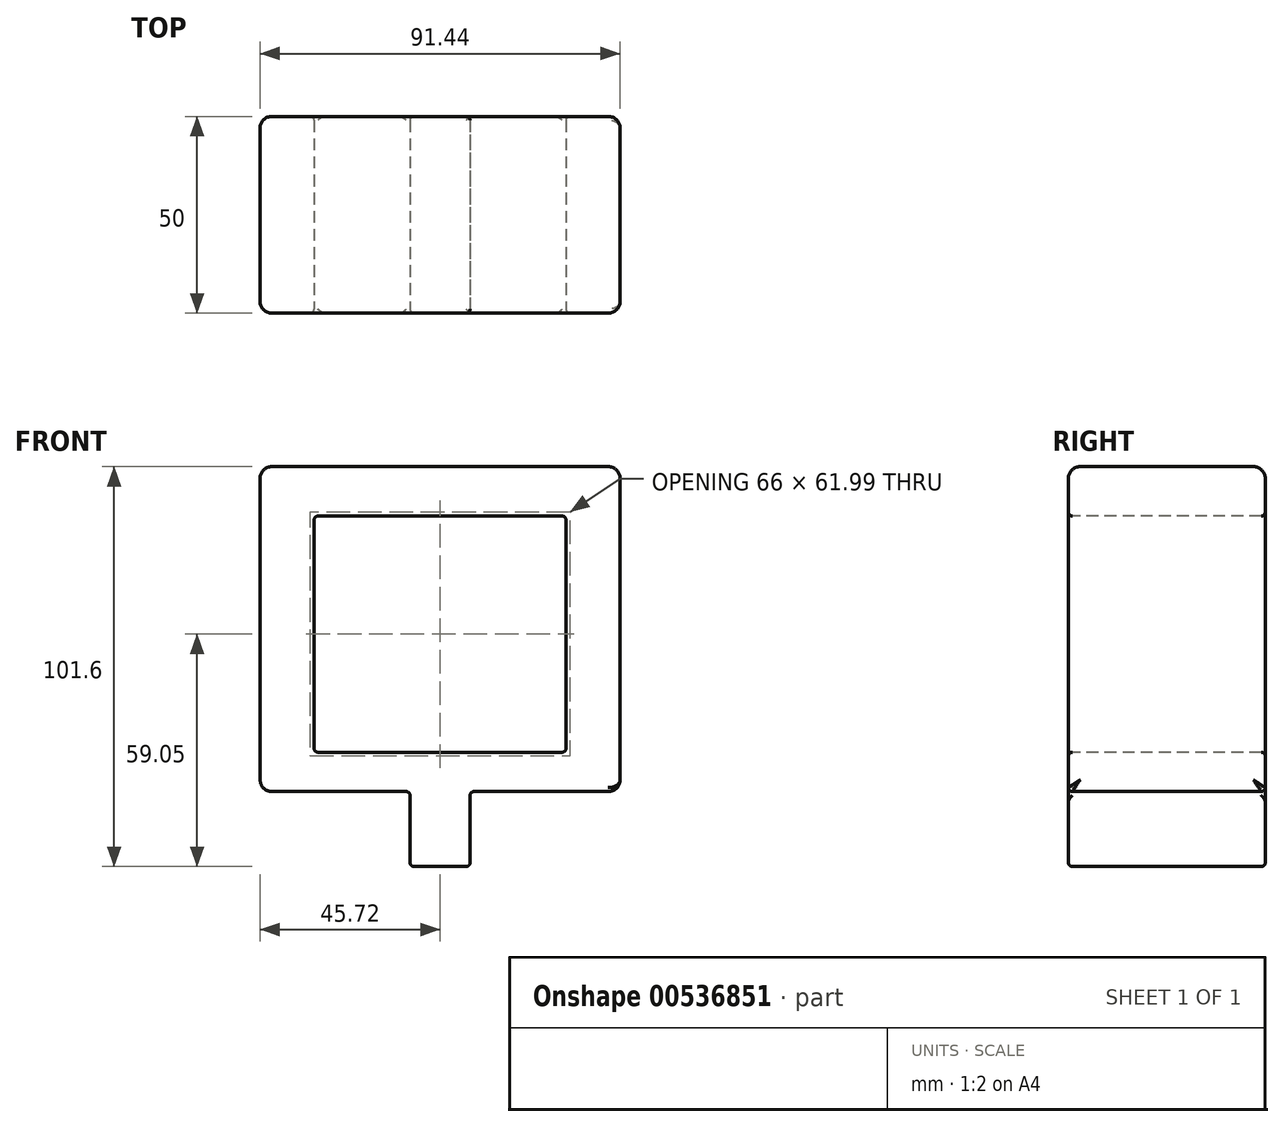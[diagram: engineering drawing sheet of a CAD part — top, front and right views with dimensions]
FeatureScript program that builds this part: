
annotation { "Feature Type Name" : "Feature", "Feature Type Description" : "" }
export const myFeature = defineFeature(function(context is Context, id is Id, definition is map)
    precondition{}
    {
        {
            var Q0;
            Q0=qCreatedBy(makeId("Front.planeOp"),FACE);
            var sketch = newSketch(context, id + "F0", { "sketchPlane" : qUnion([Q0])});
            skLineSegment(sketch, "E0", {"start": v(0, 0) * mm, "end": v(-7.62, 0) * mm});
            skLineSegment(sketch, "E1", {"start": v(-7.62, 0) * mm, "end": v(-7.62, 19.05) * mm});
            skLineSegment(sketch, "E2", {"start": v(-7.62, 19.05) * mm, "end": v(-45.72, 19.05) * mm});
            skLineSegment(sketch, "E3", {"start": v(-45.72, 19.05) * mm, "end": v(-45.72, 101.6) * mm});
            skLineSegment(sketch, "E4", {"start": v(-45.72, 101.6) * mm, "end": v(0, 101.6) * mm});
            skLineSegment(sketch, "E5", {"start": v(0, 101.6) * mm, "end": v(0, 0) * mm});
            skLineSegment(sketch, "E6.MirrorCS", {"start": v(45.72, 101.6) * mm, "end": v(0, 101.6) * mm});
            skLineSegment(sketch, "E7.MirrorCS", {"start": v(45.72, 19.05) * mm, "end": v(45.72, 101.6) * mm});
            skLineSegment(sketch, "E8.MirrorCS", {"start": v(7.62, 19.05) * mm, "end": v(45.72, 19.05) * mm});
            skLineSegment(sketch, "E9.MirrorCS", {"start": v(7.62, 0) * mm, "end": v(7.62, 19.05) * mm});
            skLineSegment(sketch, "E10.MirrorCS", {"start": v(0, 0) * mm, "end": v(7.62, 0) * mm});
            skSolve(sketch);
        }
        {
            var Q0;
            Q0 = qSketchRegion(id + "F0", true);
            extrude(context, id + "F1", {"entities" : qUnion([Q0]), "oppositeDirection" : true, "depth" : 50 * mm, "offsetDistance" : 25 * mm});
        }
        {
            var Q0;
            Q0=makeQuery(id+"F1.opExtrude","CAP_FACE",FACE,{"disambiguationData":[OSD([sQuery(id+"F0.wireOp",EDGE,"E0"),sQuery(id+"F0.wireOp",EDGE,"E1"),sQuery(id+"F0.wireOp",EDGE,"E2"),sQuery(id+"F0.wireOp",EDGE,"E3"),sQuery(id+"F0.wireOp",EDGE,"E4"),sQuery(id+"F0.wireOp",EDGE,"E6.MirrorCS"),sQuery(id+"F0.wireOp",EDGE,"E7.MirrorCS"),sQuery(id+"F0.wireOp",EDGE,"E8.MirrorCS"),sQuery(id+"F0.wireOp",EDGE,"E9.MirrorCS"),sQuery(id+"F0.wireOp",EDGE,"E10.MirrorCS")])],"isStart":true});
            var sketch = newSketch(context, id + "F2", { "sketchPlane" : qUnion([Q0])});
            skLineSegment(sketch, "E11", {"start": v(0, 29.05) * mm, "end": v(-32, 29.05) * mm});
            skLineSegment(sketch, "E12", {"start": v(-32, 29.05) * mm, "end": v(-32, 89.05) * mm});
            skLineSegment(sketch, "E13", {"start": v(-32, 89.05) * mm, "end": v(0, 89.05) * mm});
            skLineSegment(sketch, "E14.MirrorCS", {"start": v(32, 89.05) * mm, "end": v(0, 89.05) * mm});
            skLineSegment(sketch, "E15.MirrorCS", {"start": v(32, 29.05) * mm, "end": v(32, 89.05) * mm});
            skLineSegment(sketch, "E16.MirrorCS", {"start": v(0, 29.05) * mm, "end": v(32, 29.05) * mm});
            skSolve(sketch);
        }
        {
            var Q0;
            Q0 = qSketchRegion(id + "F2", true);
            extrude(context, id + "F3", {"entities" : qUnion([Q0]), "operationType" : NewBodyOperationType.REMOVE, "endBound" : BoundingType.THROUGH_ALL, "oppositeDirection" : true, "depth" : 25 * mm, "offsetDistance" : 25 * mm});
        }
        {
            var Q0;
            Q0=makeQuery(id+"F1.opExtrude","SWEPT_FACE",FACE,{"disambiguationData":[OSD([sQuery(id+"F0.wireOp",EDGE,"E4"),sQuery(id+"F0.wireOp",EDGE,"E6.MirrorCS")])]});
            var Q1;
            Q1=makeQuery(id+"F1.opExtrude","SWEPT_FACE",FACE,{"disambiguationData":[OSD([sQuery(id+"F0.wireOp",EDGE,"E7.MirrorCS")])]});
            var Q2;
            Q2=makeQuery(id+"F1.opExtrude","SWEPT_FACE",FACE,{"disambiguationData":[OSD([sQuery(id+"F0.wireOp",EDGE,"E3")])]});
            fillet(context, id + "F4", {"entities" : qUnion([Q0, Q1, Q2]), "radius" : 3 * mm, "tangentPropagation" : true, "allowEdgeOverflow" : false});
        }
        {
            var Q0;
            Q0=makeQuery(id+"F1.opExtrude","SWEPT_FACE",FACE,{"disambiguationData":[OSD([sQuery(id+"F0.wireOp",EDGE,"E1")])]});
            var Q1;
            Q1=makeQuery(id+"F1.opExtrude","SWEPT_FACE",FACE,{"disambiguationData":[OSD([sQuery(id+"F0.wireOp",EDGE,"E8.MirrorCS")])]});
            var Q2;
            Q2=makeQuery(id+"F1.opExtrude","SWEPT_FACE",FACE,{"disambiguationData":[OSD([sQuery(id+"F0.wireOp",EDGE,"E0"),sQuery(id+"F0.wireOp",EDGE,"E10.MirrorCS")])]});
            var Q3;
            Q3=makeQuery(id+"F3.boolean.opBoolean","COPY",FACE,{"derivedFrom":makeQuery(id+"F3.opExtrude","SWEPT_FACE",FACE,{"disambiguationData":[OSD([sQuery(id+"F2.wireOp",EDGE,"E12")])]})});
            var Q4;
            Q4=makeQuery(id+"F3.boolean.opBoolean","COPY",FACE,{"derivedFrom":makeQuery(id+"F3.opExtrude","SWEPT_FACE",FACE,{"disambiguationData":[OSD([sQuery(id+"F2.wireOp",EDGE,"E15.MirrorCS")])]})});
            fillet(context, id + "F5", {"entities" : qUnion([Q0, Q1, Q2, Q3, Q4]), "radius" : 1 * mm, "tangentPropagation" : true, "allowEdgeOverflow" : false});
        }
    });
